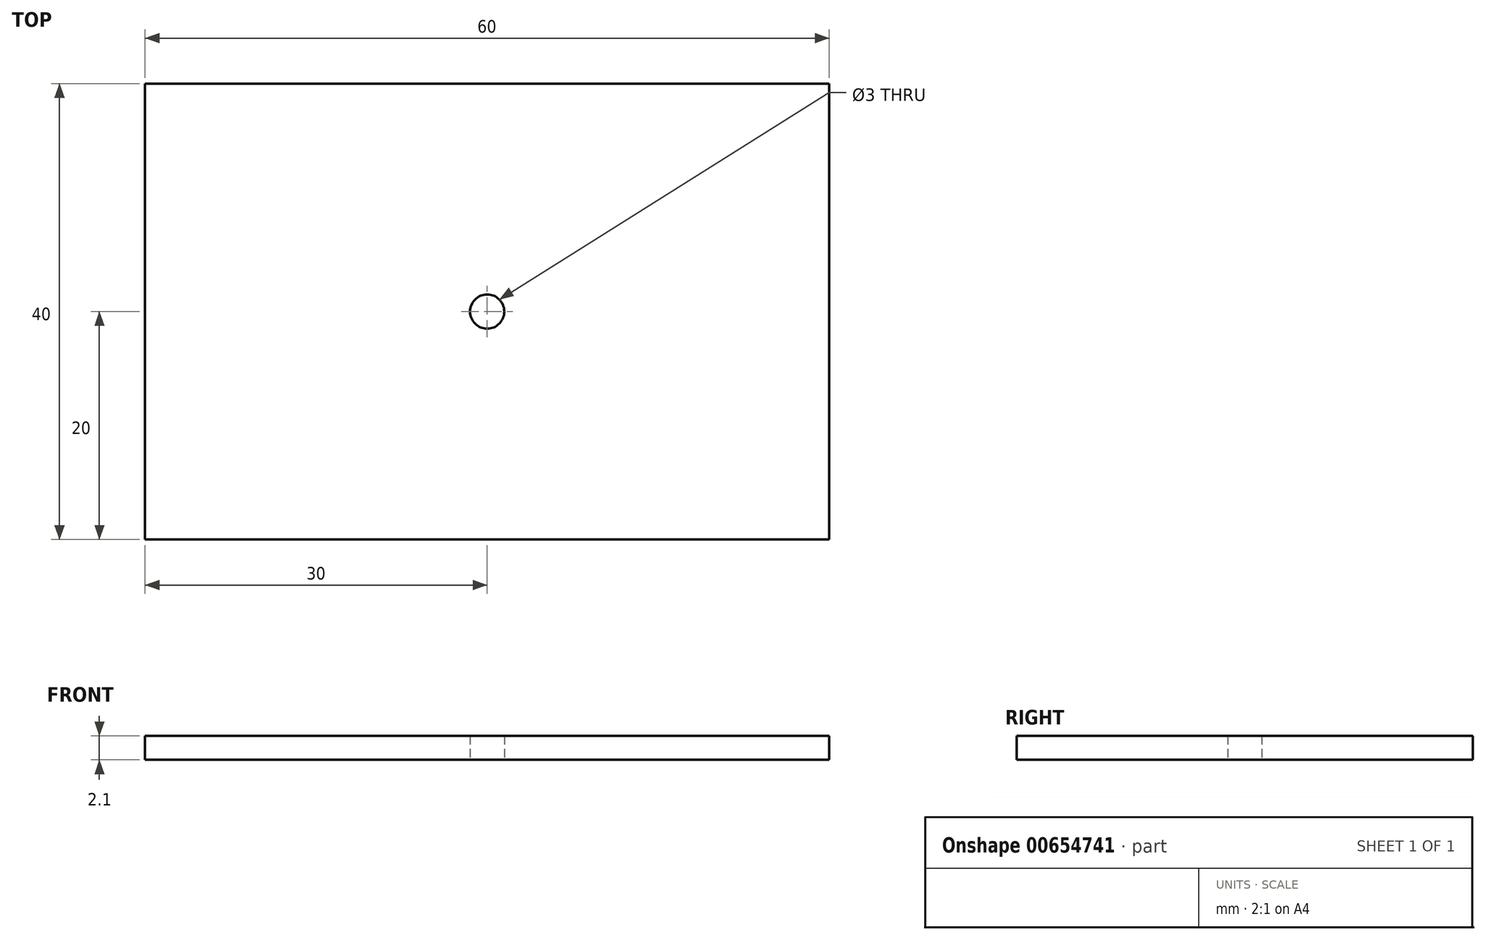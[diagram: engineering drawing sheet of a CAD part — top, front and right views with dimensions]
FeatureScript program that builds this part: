
annotation { "Feature Type Name" : "Feature", "Feature Type Description" : "" }
export const myFeature = defineFeature(function(context is Context, id is Id, definition is map)
    precondition{}
    {
        {
            var Q0;
            Q0=qCreatedBy(makeId("Top.planeOp"),FACE);
            var sketch = newSketch(context, id + "F0", { "sketchPlane" : qUnion([Q0])});
            skLineSegment(sketch, "E0.bottom", {"start": v(0, 0) * mm, "end": v(-60, 0) * mm});
            skLineSegment(sketch, "E0.top", {"start": v(0, 40) * mm, "end": v(-60, 40) * mm});
            skLineSegment(sketch, "E0.left", {"start": v(0, 0) * mm, "end": v(0, 40) * mm});
            skLineSegment(sketch, "E0.right", {"start": v(-60, 0) * mm, "end": v(-60, 40) * mm});
            skCircle(sketch, "E1", {"center": v(-30, 20) * mm, "radius": 1.5 * mm});
            skSolve(sketch);
        }
        {
            var Q0;
            Q0=makeQuery(id+"F0.imprint","IMPRINT",FACE,{"disambiguationData":[TD([[makeQuery(id+"F0.imprint","IMPRINT",EDGE,{"derivedFrom":sQuery(id+"F0.wireOp",EDGE,"E0.bottom")}),-1.0]])]});
            extrude(context, id + "F1", {"entities" : qUnion([Q0]), "depth" : 2.1 * mm, "offsetDistance" : 25 * mm});
        }
    });
